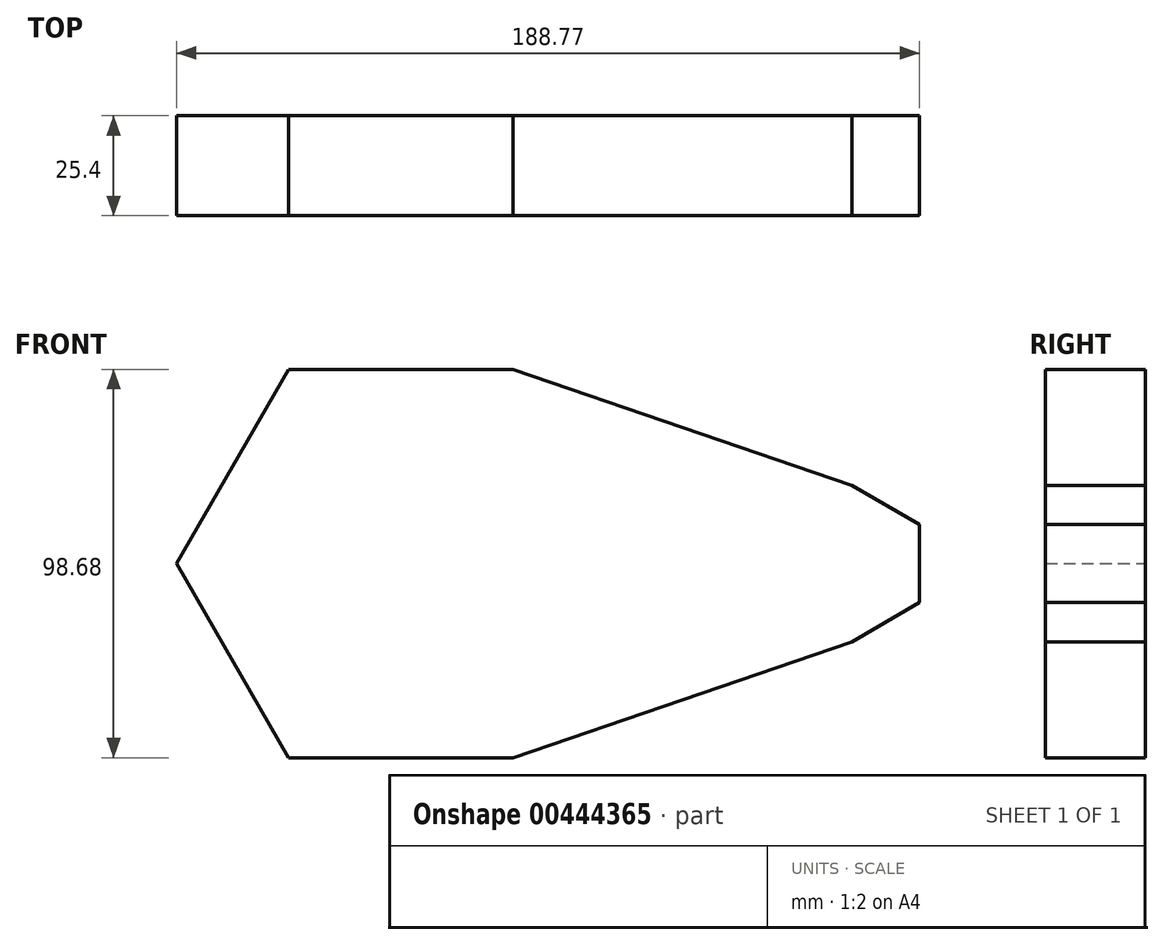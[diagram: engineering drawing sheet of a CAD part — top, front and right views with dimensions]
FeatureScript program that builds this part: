
annotation { "Feature Type Name" : "Feature", "Feature Type Description" : "" }
export const myFeature = defineFeature(function(context is Context, id is Id, definition is map)
    precondition{}
    {
        {
            var Q0;
            Q0=qCreatedBy(makeId("Front.planeOp"),FACE);
            var sketch = newSketch(context, id + "F0", { "sketchPlane" : qUnion([Q0])});
            skCircle(sketch, "E0.cCircle", {"center": v(-54, 0) * mm, "radius": 49.34 * mm, "construction": true});
            skLineSegment(sketch, "E0.0", {"start": v(-82.49, 49.34) * mm, "end": v(-25.52, 49.34) * mm});
            skLineSegment(sketch, "E0.1", {"start": v(-25.52, 49.34) * mm, "end": v(2.97, 0) * mm});
            skLineSegment(sketch, "E0.2", {"start": v(2.97, 0) * mm, "end": v(-25.52, -49.34) * mm});
            skLineSegment(sketch, "E0.3", {"start": v(-25.52, -49.34) * mm, "end": v(-82.49, -49.34) * mm});
            skLineSegment(sketch, "E0.4", {"start": v(-82.49, -49.34) * mm, "end": v(-110.97, 0) * mm});
            skLineSegment(sketch, "E0.5", {"start": v(-110.97, 0) * mm, "end": v(-82.49, 49.34) * mm});
            skPoint(sketch, "E0.0.midPoint", {"position": v(-54, 49.34) * mm});
            skCircle(sketch, "E1.cCircle", {"center": v(60.6, 0) * mm, "radius": 17.2 * mm, "construction": true});
            skLineSegment(sketch, "E1.0", {"start": v(43.38, -9.93) * mm, "end": v(43.38, 9.93) * mm});
            skLineSegment(sketch, "E1.1", {"start": v(43.38, 9.93) * mm, "end": v(60.6, 19.87) * mm});
            skLineSegment(sketch, "E1.2", {"start": v(60.6, 19.87) * mm, "end": v(77.8, 9.93) * mm});
            skLineSegment(sketch, "E1.3", {"start": v(77.8, 9.93) * mm, "end": v(77.8, -9.93) * mm});
            skLineSegment(sketch, "E1.4", {"start": v(77.8, -9.93) * mm, "end": v(60.6, -19.87) * mm});
            skLineSegment(sketch, "E1.5", {"start": v(60.6, -19.87) * mm, "end": v(43.38, -9.93) * mm});
            skPoint(sketch, "E1.0.midPoint", {"position": v(43.38, 0) * mm});
            skLineSegment(sketch, "E2", {"start": v(60.6, 19.87) * mm, "end": v(-25.52, 49.34) * mm});
            skLineSegment(sketch, "E3", {"start": v(-25.52, -49.34) * mm, "end": v(60.6, -19.87) * mm});
            skSolve(sketch);
        }
        {
            var Q0;
            Q0 = qSketchRegion(id + "F0", true);
            extrude(context, id + "F1", {"entities" : qUnion([Q0]), "depth" : 25.4 * mm});
        }
    });
